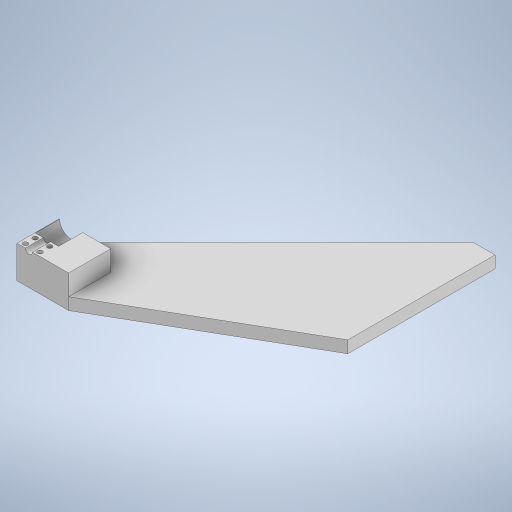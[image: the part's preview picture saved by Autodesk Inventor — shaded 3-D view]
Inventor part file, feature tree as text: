
AUTODESK INVENTOR PART (.ipt)
format: ipt  version: 2024 (Build 280153000, 153)  size: 285,184 bytes
history: native  units: mm
features: extrude x8, sketch x8
ambient origin geometry x8: Origin, YZ Plane, XZ Plane, XY Plane, X Axis, Y Axis, Z Axis, Center Point
bodies: Solid1 (feature_tree)
feature tree (16):
  extrude  "Extrusion1"  Depth=230.0mm
  extrude  "Extrusion2"  Depth=35.0mm
  extrude  "Extrusion3"  Depth=17.0mm TaperAngle=0.0deg
  extrude  "Extrusion4"  Depth=20.0mm TaperAngle=0.0deg
  extrude  "Extrusion5"  Depth=40.0mm TaperAngle=0.0deg
  extrude  "Extrusion6"  Depth=40.0mm TaperAngle=0.0deg
  extrude  "Extrusion7"  Depth=10.0mm
  extrude  "Extrusion8"  [1 undecoded]
  sketch  "Sketch1"  dims[d0=175.0mm d1=230.0mm]
  sketch  "Sketch2"  dims[d2=45.0deg d3=35.0mm]
  sketch  "Sketch3"  dims[d4=10.0mm d5=0.0mm d6=17.0mm d7=0.0mm]
  sketch  "Sketch4"  dims[d8=40.0mm d9=0.0mm d10=20.0mm d11=0.0mm]
  sketch  "Sketch5"  dims[d12=5.8mm d14=40.0mm d15=0.0mm]
  sketch  "Sketch6"  dims[d18=30.0deg d19=40.0mm d20=0.0mm]
  sketch  "Sketch7"  dims[d21=10.0mm d22=0.0mm d23=40.0mm]
  sketch  "Sketch8"  dims[d24=10.0mm d25=0.0mm]
note: 1 required parameter value undecoded (feature->parameter linkage not recoverable at this tier; creation-order binding heuristic only, values carry confidence <= 0.55)
